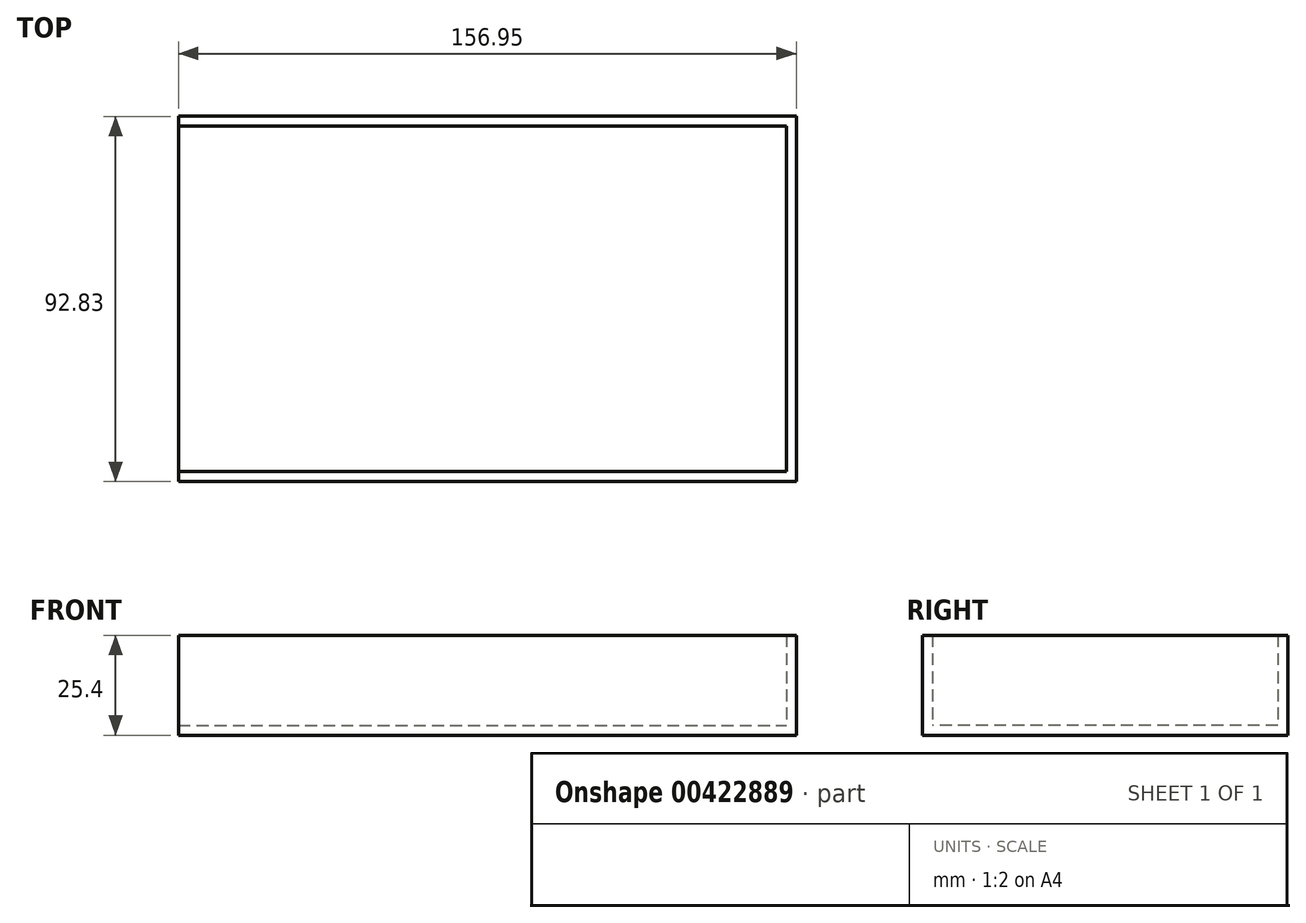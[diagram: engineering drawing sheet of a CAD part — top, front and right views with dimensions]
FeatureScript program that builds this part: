
annotation { "Feature Type Name" : "Feature", "Feature Type Description" : "" }
export const myFeature = defineFeature(function(context is Context, id is Id, definition is map)
    precondition{}
    {
        {
            var Q0;
            Q0=qCreatedBy(makeId("Top.planeOp"),FACE);
            var sketch = newSketch(context, id + "F0", { "sketchPlane" : qUnion([Q0])});
            skLineSegment(sketch, "E0.bottom", {"start": v(-80.7, 41.9) * mm, "end": v(78.8, 41.9) * mm});
            skLineSegment(sketch, "E0.top", {"start": v(-80.7, -50.94) * mm, "end": v(78.8, -50.94) * mm});
            skLineSegment(sketch, "E0.left", {"start": v(-80.7, 41.9) * mm, "end": v(-80.7, -50.94) * mm});
            skLineSegment(sketch, "E0.right", {"start": v(78.8, 41.9) * mm, "end": v(78.8, -50.94) * mm});
            skLineSegment(sketch, "E1.MirrorCS", {"start": v(-80.7, -143.77) * mm, "end": v(78.8, -143.77) * mm});
            skSolve(sketch);
        }
        {
            var Q0;
            Q0 = qSketchRegion(id + "F0", true);
            extrude(context, id + "F1", {"entities" : qUnion([Q0]), "depth" : 25.4 * mm});
        }
        {
            var Q0;
            Q0=makeQuery(id+"F1.opExtrude","CAP_FACE",FACE,{"disambiguationData":[OSD([sQuery(id+"F0.wireOp",EDGE,"E0.bottom"),sQuery(id+"F0.wireOp",EDGE,"E0.top"),sQuery(id+"F0.wireOp",EDGE,"E0.left"),sQuery(id+"F0.wireOp",EDGE,"E0.right")])],"isStart":false});
            shell(context, id + "F2", {"entities" : qUnion([Q0]), "thickness" : 2.54 * mm});
        }
        {
            var Q0;
            Q0=makeQuery(id+"F1.opExtrude","SWEPT_FACE",FACE,{"disambiguationData":[OSD([sQuery(id+"F0.wireOp",EDGE,"E0.left")])]});
            extrude(context, id + "F3", {"entities" : qUnion([Q0]), "operationType" : NewBodyOperationType.REMOVE, "oppositeDirection" : true, "depth" : 2.54 * mm});
        }
    });
